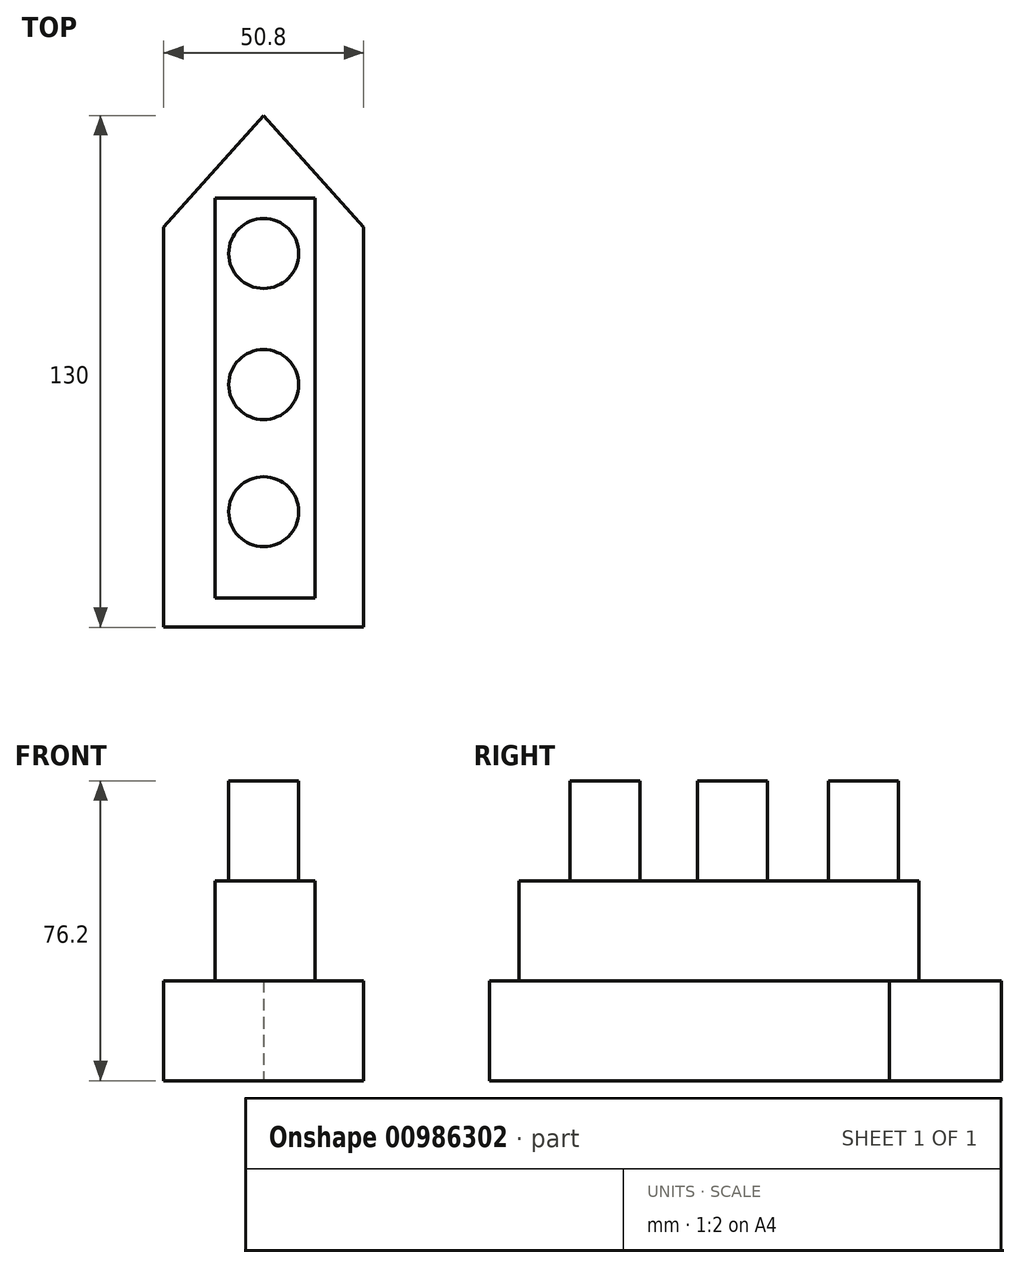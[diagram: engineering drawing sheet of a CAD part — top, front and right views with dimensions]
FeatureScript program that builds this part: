
annotation { "Feature Type Name" : "Feature", "Feature Type Description" : "" }
export const myFeature = defineFeature(function(context is Context, id is Id, definition is map)
    precondition{}
    {
        {
            var Q0;
            Q0=qCreatedBy(makeId("Top.planeOp"),FACE);
            var sketch = newSketch(context, id + "F0", { "sketchPlane" : qUnion([Q0])});
            skLineSegment(sketch, "E0", {"start": v(25.4, 37.28) * mm, "end": v(0, 65.68) * mm});
            skLineSegment(sketch, "E1", {"start": v(0, 65.68) * mm, "end": v(-25.4, 37.28) * mm});
            skLineSegment(sketch, "E2", {"start": v(-25.4, 37.28) * mm, "end": v(-25.4, -64.32) * mm});
            skLineSegment(sketch, "E3", {"start": v(-25.4, -64.32) * mm, "end": v(25.4, -64.32) * mm});
            skLineSegment(sketch, "E4", {"start": v(25.4, -64.32) * mm, "end": v(25.4, 37.28) * mm});
            skSolve(sketch);
        }
        {
            var Q0;
            Q0 = qSketchRegion(id + "F0", true);
            extrude(context, id + "F1", {"entities" : qUnion([Q0]), "depth" : 25.4 * mm, "offsetDistance" : 25.4 * mm});
        }
        {
            var Q0;
            Q0=makeQuery(id+"F1.opExtrude","CAP_FACE",FACE,{"disambiguationData":[OSD([sQuery(id+"F0.wireOp",EDGE,"E0"),sQuery(id+"F0.wireOp",EDGE,"E1"),sQuery(id+"F0.wireOp",EDGE,"E2"),sQuery(id+"F0.wireOp",EDGE,"E3"),sQuery(id+"F0.wireOp",EDGE,"E4")])],"isStart":false});
            var sketch = newSketch(context, id + "F2", { "sketchPlane" : qUnion([Q0])});
            skLineSegment(sketch, "E5.bottom", {"start": v(-12.34, 44.76) * mm, "end": v(13.06, 44.76) * mm});
            skLineSegment(sketch, "E5.top", {"start": v(-12.34, -56.84) * mm, "end": v(13.06, -56.84) * mm});
            skLineSegment(sketch, "E5.left", {"start": v(-12.34, 44.76) * mm, "end": v(-12.34, -56.84) * mm});
            skLineSegment(sketch, "E5.right", {"start": v(13.06, 44.76) * mm, "end": v(13.06, -56.84) * mm});
            skSolve(sketch);
        }
        {
            var Q0;
            Q0 = qSketchRegion(id + "F2", true);
            extrude(context, id + "F3", {"entities" : qUnion([Q0]), "operationType" : NewBodyOperationType.ADD, "depth" : 25.4 * mm, "offsetDistance" : 25.4 * mm});
        }
        {
            var Q0;
            Q0=makeQuery(id+"F3.opExtrude","CAP_FACE",FACE,{"disambiguationData":[OSD([sQuery(id+"F2.wireOp",EDGE,"E5.bottom"),sQuery(id+"F2.wireOp",EDGE,"E5.top"),sQuery(id+"F2.wireOp",EDGE,"E5.left"),sQuery(id+"F2.wireOp",EDGE,"E5.right")])],"isStart":false});
            var sketch = newSketch(context, id + "F4", { "sketchPlane" : qUnion([Q0])});
            skCircle(sketch, "E6", {"center": v(0, -34.97) * mm, "radius": 8.9 * mm});
            skCircle(sketch, "E7", {"center": v(0, -2.66) * mm, "radius": 8.9 * mm});
            skCircle(sketch, "E8", {"center": v(0, 30.65) * mm, "radius": 8.9 * mm});
            skSolve(sketch);
        }
        {
            var Q0;
            Q0 = qSketchRegion(id + "F4", true);
            extrude(context, id + "F5", {"entities" : qUnion([Q0]), "operationType" : NewBodyOperationType.ADD, "depth" : 25.4 * mm, "offsetDistance" : 25.4 * mm});
        }
    });
